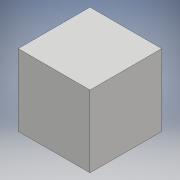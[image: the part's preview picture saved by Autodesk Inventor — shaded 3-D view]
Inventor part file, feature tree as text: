
AUTODESK INVENTOR PART (.ipt)
format: ipt  version: 2017 (Build 210142000, 142)  size: 83,968 bytes
history: native  units: mm
features: extrude x1, sketch x1
ambient origin geometry x8: Origin, YZ Plane, XZ Plane, XY Plane, X Axis, Y Axis, Z Axis, Center Point
bodies: Solid1 (feature_tree)
feature tree (2):
  extrude  "Extrusion1"  Depth=55.88mm
  sketch  "Sketch1"  dims[d0=55.88mm d1=55.88mm d2=55.88mm d3=0.0mm]
